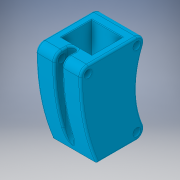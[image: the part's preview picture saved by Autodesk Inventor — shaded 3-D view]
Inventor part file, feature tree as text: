
AUTODESK INVENTOR PART (.ipt)
format: ipt  version: 2017 SP1 (Build 210196100, 196)  size: 288,256 bytes
history: native  units: in
note: dims shown in document units (in); Inventor stores cm internally (conversion verified against a paired STEP export)
features: extrude x3, fillet x3, sketch x3, chamfer x1, plane x1
ambient origin geometry x8: Origin, YZ Plane, XZ Plane, XY Plane, X Axis, Y Axis, Z Axis, Center Point
bodies: Solid1 (feature_tree)
feature tree (11):
  extrude  "Extrusion1"  Depth=3.0in TaperAngle=0.0deg
  extrude  "Extrusion2"  Depth=0.0625in
  chamfer  "Chamfer1"  Distance=0.0625in
  fillet  "Fillet1"  Radius=0.02in
  fillet  "Fillet2"  Radius=0.25in
  plane  "Work Plane2"
  extrude  "Extrusion5"  Depth=0.25in
  fillet  "Fillet4"  Radius=0.26in
  sketch  "Sketch1"  dims[d0=1.02in d3=3.0in d4=0.0in]
  sketch  "Sketch2"  dims[d9=5.0in d10=0.0in d14=0.0625in]
  sketch  "Sketch6"  dims[d16=0.25in d19=0.0625in d20=0.02in d21=0.125in d22=45.0deg d40=0.25in d45=0.25in d46=0.26in d47=0.25in d48=1.5in d49=1.125in d50=1.0in d51=0.25in d52=-0.0137in d53=0.05in d54=0.125in d55=0.5in d56=0.25in d57=0.0in d58=0.0625in d59=0.03in]
